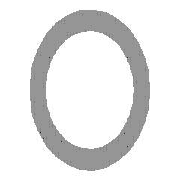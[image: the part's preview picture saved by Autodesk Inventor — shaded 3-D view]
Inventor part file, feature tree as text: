
AUTODESK INVENTOR PART (.ipt)
format: ipt  version: 2021 (Build 250183000, 183)  size: 320,000 bytes
history: native  units: mm (DEFAULTED — no unit token found)
features: other x13, plane x3, sketch x3, sweep x1, split x1
ambient origin geometry x8: Origin, YZ Plane, XZ Plane, XY Plane, X Axis, Y Axis, Z Axis, Center Point
bodies: Solid1 (feature_tree)
feature tree (21):
  parser-record x1  (decoder bookkeeping rows leaked as tree rows — omitted from the tree; the rows remain in map.json)
  other  "Driven Length"
  other  "Plano inicial"
  other  "Plano final"
  other  "Trayectoria de barrido"
  plane  "Plano de trabajo de orientación"
  sweep  "Cuerpo"
  plane  "Plano de trabajo11"
  split  "Dividir7"
  sketch  "Sketch3"  dims[d0=26.67mm d1=2.8702mm]
  plane  "Work Plane3"
  sketch  "Sketch4"  dims[d4=-0.0mm]
  other  "Sup149"
  other  "Sup150"
  other  "Sólido49"
  sketch  "Boceto11"  dims[d5=506.111834mm d6=90.0deg d7=506.111834mm d8=0.0mm d9=0.0mm d222=5.0mm d223=0.0mm d224=5.0mm d225=0.0mm d226=0.0mm d227=90.0deg d228=0.0mm d229=90.0deg]
  other  "Sup151"
  other  "SuperficieSolevación7"
  other  "Sup148"
  other  "Superficie de contorno95"
  other  "Superficie de contorno96"
